# Revit family: Shower-Bath-American_Standard-Serin-T064.602
name_source: partatom
category: Plumbing Fixtures
revit_build: Autodesk Revit 2014 (Build: 20130308_1515(x64)
units: mm (PartAtom-declared; Revit-internal decimal feet)

## types (1)
- T064.602
    ADA Compliant = Yes
    Assembly Code = D2020300
    CW Connection = Yes
    CWFU = 2
    Cold Water Connection Diameter = 1/2"
    Cold Water Connection Height = 48"
    Cold Water Connection Radius = 1/4"
    Default Elevation = 0"
    Description = Serin Pressure Balance Bath-Shower Fitting with Built-In Diverter.
    HW Connection = Yes
    HWFU = 3
    Height = 79 5/8"
    Hot Water Connection Diameter = 1/2"
    Hot Water Connection Height = 48"
    Hot Water Connection Radius = 1/4"
    Hydronic Supply Diameter = 1/2"
    Hydronic Supply Radius = 1/4"
    Length = 7 1/4"
    Manufacturer = American Standard
    Material = Brass-American Standard-002-Polished Chrome
    Model = T064.602
    Price = Prices may vary. Please consult Manufacturer Representative for most up-to-date price list.
    Product Documentation Link = https://www.americanstandard-us.com
    Product Page URL = https://www.americanstandard-us.com
    URL = http://www.americanstandard-us.com
    Vent Connection = No
    WFU = 4
    Warranty Information = Limited Lifetime Function and Finish Warranty.
    Waste Connection = No
    Width = 6 3/4"

## geometry (parser evidence)
native form markers: Sweep x2
no freeform markers — native parametric forms only
